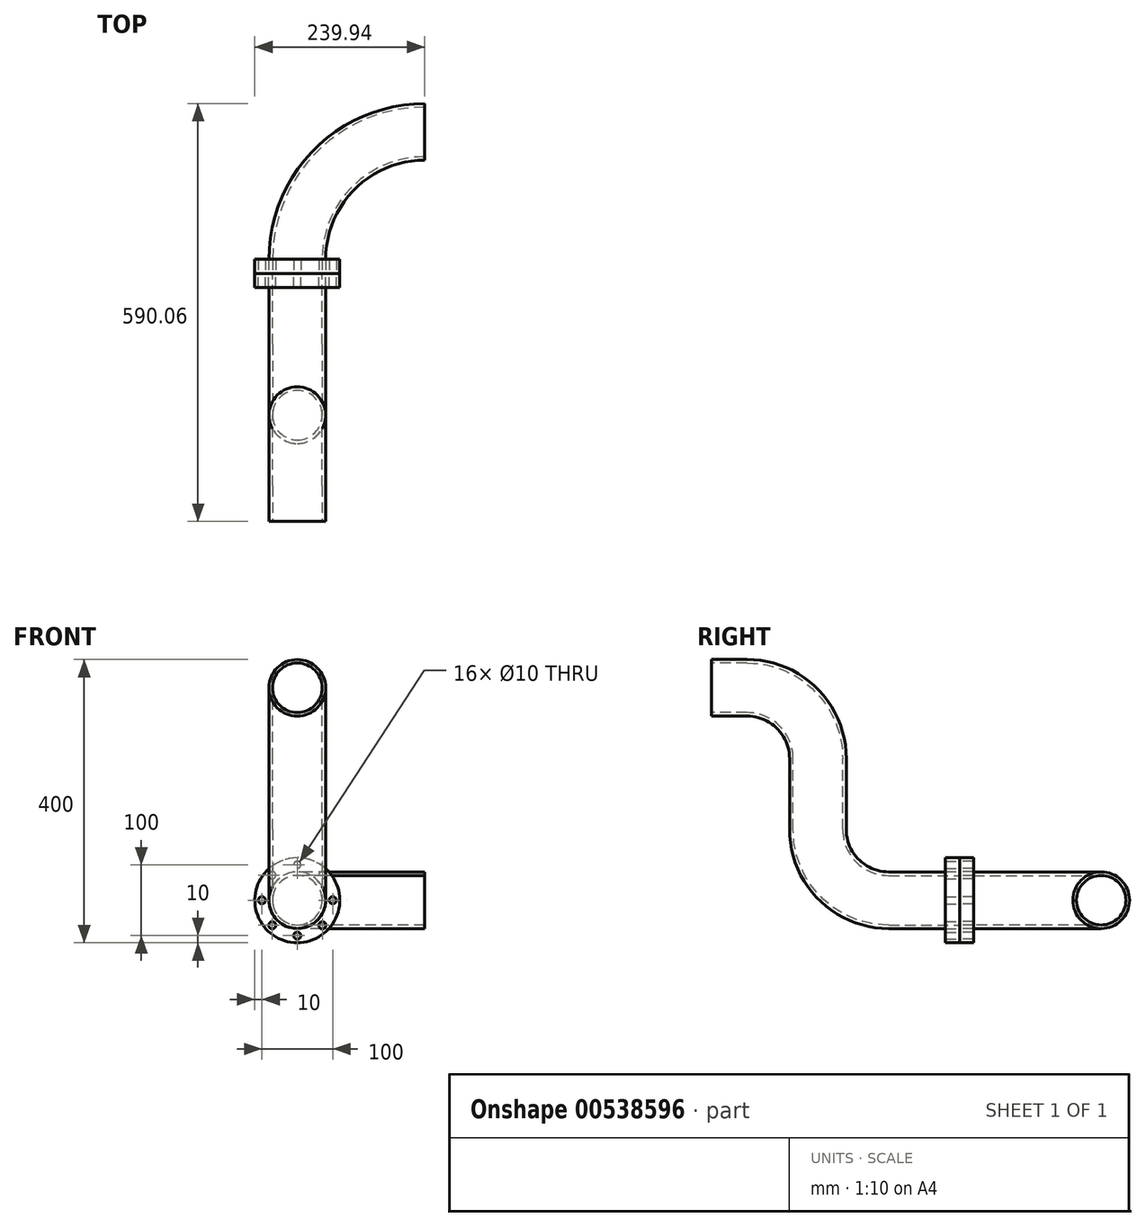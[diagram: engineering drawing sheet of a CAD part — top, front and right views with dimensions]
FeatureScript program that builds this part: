
annotation { "Feature Type Name" : "Feature", "Feature Type Description" : "" }
export const myFeature = defineFeature(function(context is Context, id is Id, definition is map)
    precondition{}
    {
        {
            var Q0;
            Q0=qCreatedBy(makeId("Front.planeOp"),FACE);
            var sketch = newSketch(context, id + "F0", { "sketchPlane" : qUnion([Q0])});
            skCircle(sketch, "E0", {"center": v(0, 0) * mm, "radius": 60 * mm});
            skCircle(sketch, "E1", {"center": v(0, 50) * mm, "radius": 5 * mm});
            skCircle(sketch, "E2.1.0", {"center": v(-35.36, 35.36) * mm, "radius": 5 * mm});
            skCircle(sketch, "E2.2.0", {"center": v(-50, 0) * mm, "radius": 5 * mm});
            skCircle(sketch, "E3.1.3.0", {"center": v(-35.36, -35.36) * mm, "radius": 5 * mm});
            skCircle(sketch, "E3.1.4.0", {"center": v(0, -50) * mm, "radius": 5 * mm});
            skCircle(sketch, "E3.1.5.0", {"center": v(35.36, -35.36) * mm, "radius": 5 * mm});
            skCircle(sketch, "E3.1.6.0", {"center": v(50, 0) * mm, "radius": 5 * mm});
            skCircle(sketch, "E3.1.7.0", {"center": v(35.36, 35.36) * mm, "radius": 5 * mm});
            skCircle(sketch, "E4", {"center": v(0, 0) * mm, "radius": 35 * mm});
            skSolve(sketch);
        }
        {
            var Q0;
            Q0 = qSketchRegion(id + "F0", true);
            var Q1;
            Q1 = qSketchRegion(id + "F2", true);
            extrude(context, id + "F1", {"entities" : qUnion([Q0, Q1]), "depth" : 20 * mm, "offsetDistance" : 25 * mm});
        }
        {
            var Q0;
            Q0=qCreatedBy(makeId("Front.planeOp"),FACE);
            var sketch = newSketch(context, id + "F2", { "sketchPlane" : qUnion([Q0])});
            skCircle(sketch, "E5", {"center": v(0, 0) * mm, "radius": 40 * mm});
            skCircle(sketch, "E6", {"center": v(0, 0) * mm, "radius": 35 * mm});
            skSolve(sketch);
        }
        {
            var Q0;
            Q0=qCreatedBy(makeId("Right.planeOp"),FACE);
            var sketch = newSketch(context, id + "F3", { "sketchPlane" : qUnion([Q0])});
            skLineSegment(sketch, "E7", {"start": v(0, 0) * mm, "end": v(-100, 0) * mm});
            skLineSegment(sketch, "E8", {"start": v(-200, 100) * mm, "end": v(-200, 200) * mm});
            skLineSegment(sketch, "E9", {"start": v(-300, 300) * mm, "end": v(-350, 300) * mm});
            skPoint(sketch, "E10.visualSharp", {"position": v(-200, 0) * mm});
            skArc(sketch, "E10.filletArc", {"start": v(-200, 100) * mm, "mid": v(-170.71, 29.29) * mm, "end": v(-100, 0) * mm});
            skPoint(sketch, "E11.visualSharp", {"position": v(-200, 300) * mm});
            skArc(sketch, "E11.filletArc", {"start": v(-200, 200) * mm, "mid": v(-229.29, 270.71) * mm, "end": v(-300, 300) * mm});
            skSolve(sketch);
        }
        {
            var Q0;
            Q0=makeQuery(id+"F2.imprint","IMPRINT",FACE,{"disambiguationData":[TD([[makeQuery(id+"F2.imprint","IMPRINT",EDGE,{"derivedFrom":sQuery(id+"F2.wireOp",EDGE,"E5")}),1.0]])]});
            var Q1;
            Q1=sQuery(id+"F3.wireOp",EDGE,"E7");
            var Q2;
            Q2=sQuery(id+"F3.wireOp",EDGE,"E10.filletArc");
            var Q3;
            Q3=sQuery(id+"F3.wireOp",EDGE,"E8");
            var Q4;
            Q4=sQuery(id+"F3.wireOp",EDGE,"E11.filletArc");
            var Q5;
            Q5=sQuery(id+"F3.wireOp",EDGE,"E9");
            sweep(context, id + "F4", {"operationType" : NewBodyOperationType.ADD, "profiles" : qUnion([Q0]), "path" : qUnion([Q1, Q2, Q3, Q4, Q5])});
        }
        {
            var Q0;
            Q0=makeQuery(id+"F0.imprint","IMPRINT",FACE,{"disambiguationData":[TD([[makeQuery(id+"F0.imprint","IMPRINT",EDGE,{"derivedFrom":sQuery(id+"F0.wireOp",EDGE,"E0")}),1.0]])]});
            extrude(context, id + "F5", {"entities" : qUnion([Q0]), "oppositeDirection" : true, "depth" : 20 * mm, "offsetDistance" : 25 * mm});
        }
        {
            var Q0;
            Q0=makeQuery(id+"F5.opExtrude","CAP_FACE",FACE,{"disambiguationData":[OSD([sQuery(id+"F0.wireOp",EDGE,"E0"),sQuery(id+"F0.wireOp",EDGE,"E1"),sQuery(id+"F0.wireOp",EDGE,"E2.1.0"),sQuery(id+"F0.wireOp",EDGE,"E2.2.0"),sQuery(id+"F0.wireOp",EDGE,"E3.1.3.0"),sQuery(id+"F0.wireOp",EDGE,"E3.1.4.0"),sQuery(id+"F0.wireOp",EDGE,"E3.1.5.0"),sQuery(id+"F0.wireOp",EDGE,"E3.1.6.0"),sQuery(id+"F0.wireOp",EDGE,"E3.1.7.0"),sQuery(id+"F0.wireOp",EDGE,"E4")])],"isStart":false});
            var sketch = newSketch(context, id + "F6", { "sketchPlane" : qUnion([Q0])});
            skCircle(sketch, "E12", {"center": v(0, 0) * mm, "radius": 35 * mm});
            skCircle(sketch, "E13", {"center": v(0, 0) * mm, "radius": 40 * mm});
            skSolve(sketch);
        }
        {
            var Q0;
            Q0=qCreatedBy(makeId("Top.planeOp"),FACE);
            var sketch = newSketch(context, id + "F7", { "sketchPlane" : qUnion([Q0])});
            skLineSegment(sketch, "E14", {"start": v(0, 0) * mm, "end": v(0, 20.06) * mm, "construction": true});
            skLineSegment(sketch, "E15", {"start": v(0, 20.06) * mm, "end": v(180, 20.06) * mm, "construction": true});
            skLineSegment(sketch, "E16", {"start": v(180, 20.06) * mm, "end": v(180, 200.06) * mm, "construction": true});
            skArc(sketch, "E17", {"start": v(180, 200.06) * mm, "mid": v(52.72, 147.34) * mm, "end": v(0, 20.06) * mm});
            skSolve(sketch);
        }
        {
            var Q0;
            Q0=makeQuery(id+"F6.imprint","IMPRINT",FACE,{"disambiguationData":[TD([[makeQuery(id+"F6.imprint","IMPRINT",EDGE,{"derivedFrom":sQuery(id+"F6.wireOp",EDGE,"E12")}),1.0]])]});
            var Q1;
            Q1=sQuery(id+"F7.wireOp",EDGE,"E17");
            sweep(context, id + "F8", {"operationType" : NewBodyOperationType.ADD, "profiles" : qUnion([Q0]), "path" : qUnion([Q1])});
        }
    });
